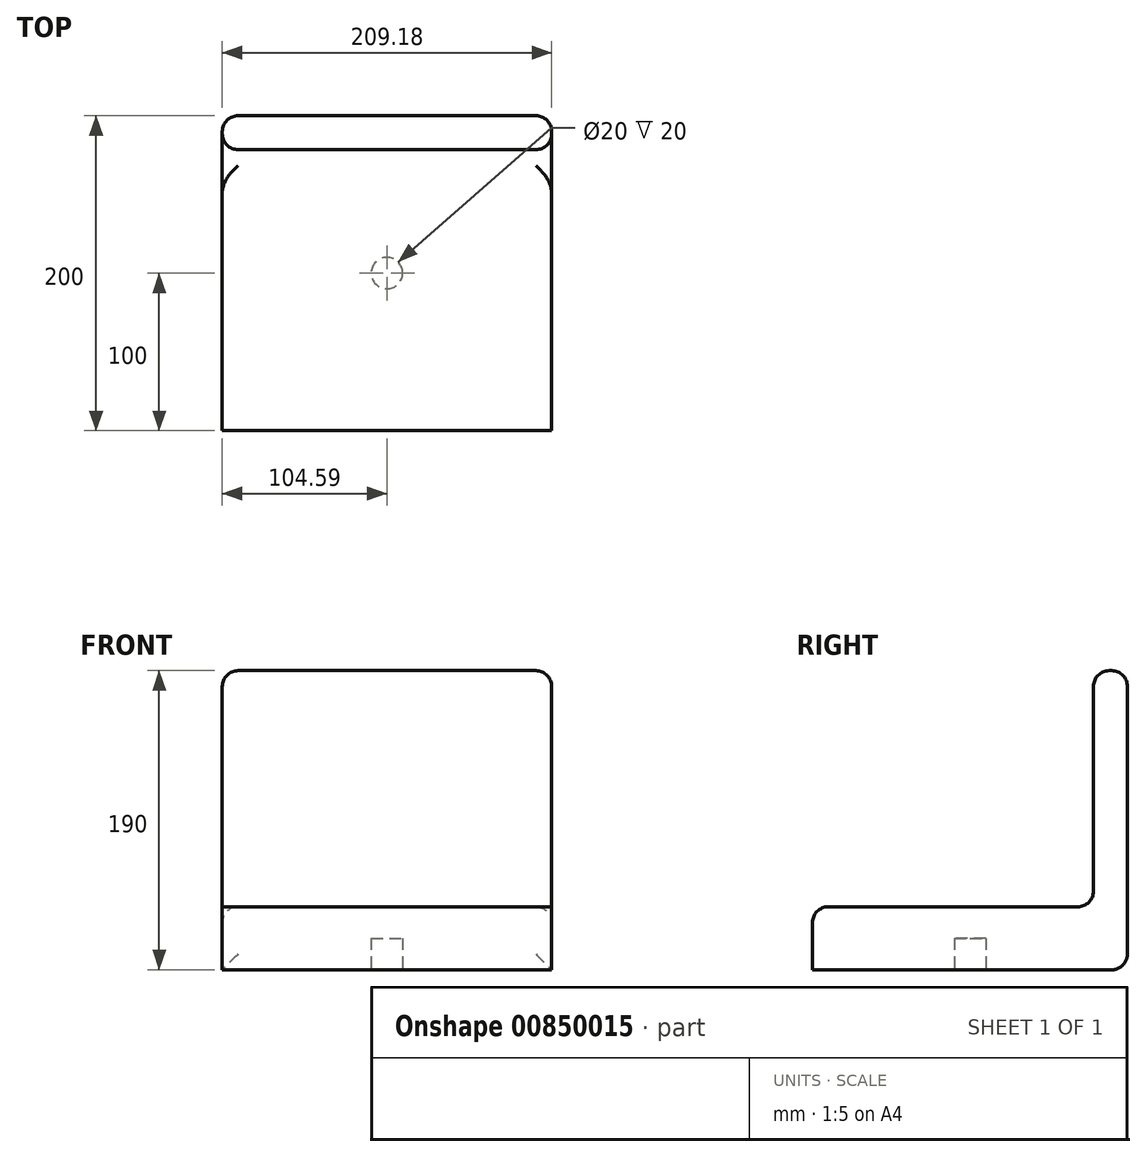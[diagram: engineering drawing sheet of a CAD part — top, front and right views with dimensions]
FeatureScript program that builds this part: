
annotation { "Feature Type Name" : "Feature", "Feature Type Description" : "" }
export const myFeature = defineFeature(function(context is Context, id is Id, definition is map)
    precondition{}
    {
        {
            var Q0;
            Q0=qCreatedBy(makeId("Top.planeOp"),FACE);
            var sketch = newSketch(context, id + "F0", { "sketchPlane" : qUnion([Q0])});
            skLineSegment(sketch, "E0.bottom", {"start": v(104.59, -100) * mm, "end": v(-104.59, -100) * mm});
            skLineSegment(sketch, "E0.top", {"start": v(104.59, 100) * mm, "end": v(-104.59, 100) * mm});
            skLineSegment(sketch, "E0.left", {"start": v(104.59, -100) * mm, "end": v(104.59, 100) * mm});
            skLineSegment(sketch, "E0.right", {"start": v(-104.59, -100) * mm, "end": v(-104.59, 100) * mm});
            skPoint(sketch, "E0.middle", {"position": v(0, 0) * mm});
            skSolve(sketch);
        }
        {
            var Q0;
            Q0=makeQuery(id+"F0.imprint","IMPRINT",FACE,{"disambiguationData":[TD([[makeQuery(id+"F0.imprint","IMPRINT",EDGE,{"derivedFrom":sQuery(id+"F0.wireOp",EDGE,"E0.bottom")}),-1.0]])]});
            extrude(context, id + "F1", {"entities" : qUnion([Q0]), "depth" : 40 * mm, "offsetDistance" : 25 * mm});
        }
        {
            var Q0;
            Q0=makeQuery(id+"F1.opExtrude","CAP_FACE",FACE,{"disambiguationData":[OSD([sQuery(id+"F0.wireOp",EDGE,"E0.bottom"),sQuery(id+"F0.wireOp",EDGE,"E0.top"),sQuery(id+"F0.wireOp",EDGE,"E0.left"),sQuery(id+"F0.wireOp",EDGE,"E0.right")])],"isStart":false});
            var sketch = newSketch(context, id + "F2", { "sketchPlane" : qUnion([Q0])});
            skLineSegment(sketch, "E1", {"start": v(104.59, 78.44) * mm, "end": v(-104.59, 78.44) * mm});
            skSolve(sketch);
        }
        {
            var Q0;
            {var subQ0=sQuery(id+"F2.wireOp",EDGE,"E1");Q0=makeQuery(id+"F2.imprint","IMPRINT",FACE,{"disambiguationData":[TD([[makeQuery(id+"F2.imprint","IMPRINT",EDGE,{"derivedFrom":subQ0}),-1.0]])]});}
            extrude(context, id + "F3", {"entities" : qUnion([Q0]), "operationType" : NewBodyOperationType.ADD, "depth" : 150 * mm, "offsetDistance" : 25 * mm});
        }
        {
            var Q0;
            Q0=makeQuery(id+"F1.opExtrude","CAP_FACE",FACE,{"disambiguationData":[OSD([sQuery(id+"F0.wireOp",EDGE,"E0.bottom"),sQuery(id+"F0.wireOp",EDGE,"E0.top"),sQuery(id+"F0.wireOp",EDGE,"E0.left"),sQuery(id+"F0.wireOp",EDGE,"E0.right")])],"isStart":true});
            var sketch = newSketch(context, id + "F4", { "sketchPlane" : qUnion([Q0])});
            skCircle(sketch, "E2", {"center": v(0, 0) * mm, "radius": 10 * mm});
            skSolve(sketch);
        }
        {
            var Q0;
            Q0=makeQuery(id+"F4.imprint","IMPRINT",FACE,{"disambiguationData":[TD([[makeQuery(id+"F4.imprint","IMPRINT",EDGE,{"derivedFrom":sQuery(id+"F4.wireOp",EDGE,"E2")}),1.0]])]});
            extrude(context, id + "F5", {"entities" : qUnion([Q0]), "operationType" : NewBodyOperationType.REMOVE, "oppositeDirection" : true, "depth" : 20 * mm, "offsetDistance" : 25 * mm});
        }
        {
            var Q0;
            Q0=makeQuery(id+"F3.opExtrude","CAP_EDGE",EDGE,{"disambiguationData":[OSD([sQuery(id+"F2.wireOp",EDGE,"E1")])],"isStart":false});
            var Q1;
            Q1=makeQuery(id+"F3.opExtrude","CAP_EDGE",EDGE,{"disambiguationData":[OSD([sQuery(id+"F0.wireOp",EDGE,"E0.top")])],"isStart":false});
            var Q2;
            Q2=makeQuery(id+"F3.opExtrude","CAP_EDGE",EDGE,{"disambiguationData":[OSD([sQuery(id+"F0.wireOp",EDGE,"E0.right")])],"isStart":false});
            var Q3;
            Q3=makeQuery(id+"F3.opExtrude","CAP_EDGE",EDGE,{"disambiguationData":[OSD([sQuery(id+"F0.wireOp",EDGE,"E0.left")])],"isStart":false});
            var Q4;
            Q4=makeQuery(id+"F3.opExtrude","SWEPT_FACE",FACE,{"disambiguationData":[OSD([sQuery(id+"F2.wireOp",EDGE,"E1")])]});
            var Q5;
            {var subQ0=sQuery(id+"F0.wireOp",EDGE,"E0.top");Q5=makeQuery(id+"F3.boolean.opBoolean","MERGE",FACE,{"derivedFrom":[makeQuery(id+"F1.opExtrude","SWEPT_FACE",FACE,{"disambiguationData":[OSD([subQ0])]}),makeQuery(id+"F3.opExtrude","SWEPT_FACE",FACE,{"disambiguationData":[OSD([subQ0])]})]});}
            fillet(context, id + "F6", {"entities" : qUnion([Q0, Q1, Q2, Q3, Q4, Q5]), "radius" : 10 * mm, "tangentPropagation" : true, "allowEdgeOverflow" : false});
        }
        {
            var Q0;
            Q0=makeQuery(id+"F1.opExtrude","CAP_EDGE",EDGE,{"disambiguationData":[OSD([sQuery(id+"F0.wireOp",EDGE,"E0.bottom")])],"isStart":false});
            fillet(context, id + "F7", {"entities" : qUnion([Q0]), "radius" : 10 * mm, "tangentPropagation" : true, "allowEdgeOverflow" : false});
        }
    });
